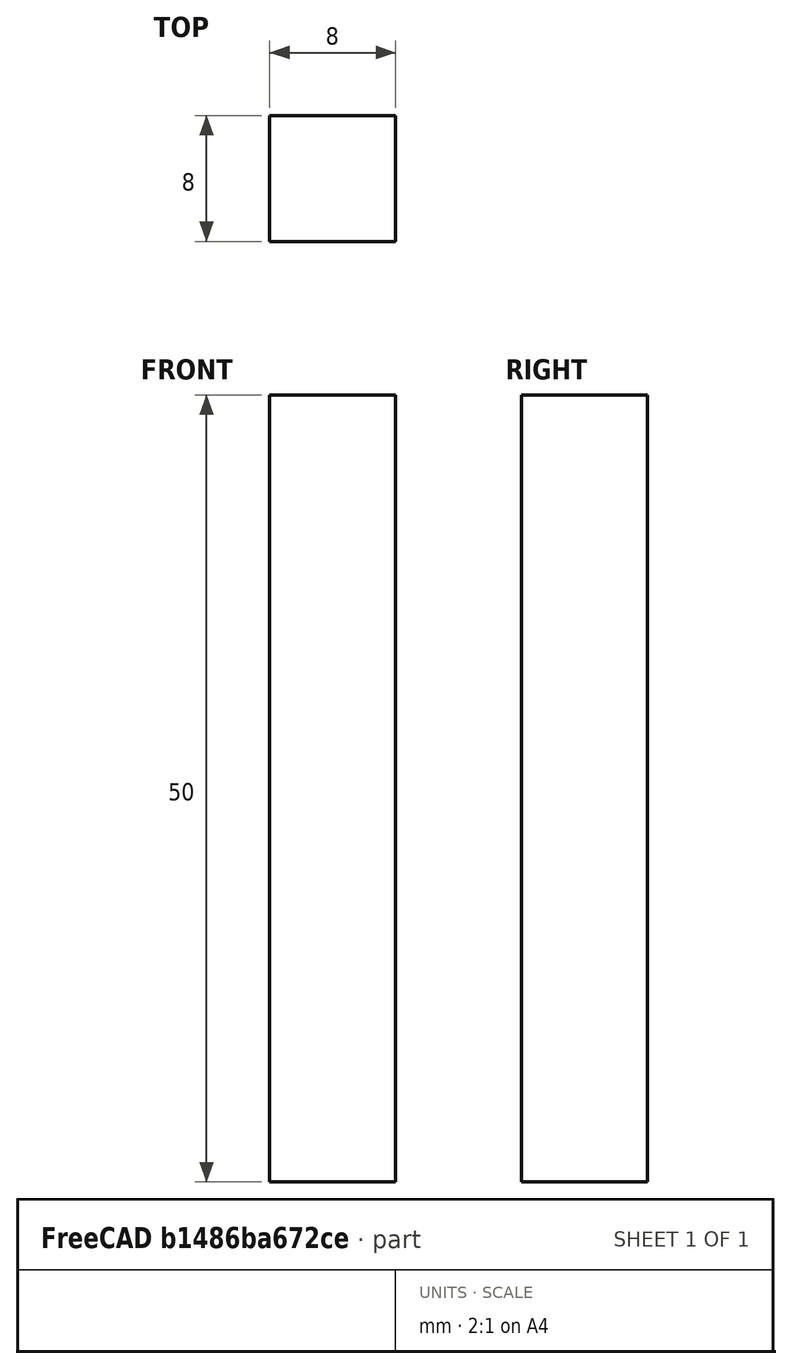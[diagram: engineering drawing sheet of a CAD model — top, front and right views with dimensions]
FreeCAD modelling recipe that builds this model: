
FCSTD DOCUMENT  (FreeCAD 0.15R4671 (Git))
Label: Square Bar 8 EN10059 S235JR
License: All rights reserved
LicenseURL: http://en.wikipedia.org/wiki/All_rights_reserved
objects: Sketcher::SketchObject×1, Part::Extrusion×1
note: 2 computed .brp shape members not serialized (recipe doc carries the construction recipe); baked Part::Feature solids carry a one-line shape summary decoded from their .brp

FEATURE [Sketcher::SketchObject] Sketch
  sketch-geometry (4):
    g0: LineSegment StartX=-4 StartY=-4 StartZ=0 EndX=4 EndY=-4 EndZ=0
    g1: LineSegment StartX=4 StartY=-4 StartZ=0 EndX=4 EndY=4 EndZ=0
    g2: LineSegment StartX=4 StartY=4 StartZ=0 EndX=-4 EndY=4 EndZ=0
    g3: LineSegment StartX=-4 StartY=4 StartZ=0 EndX=-4 EndY=-4 EndZ=0
  constraints (12):
    c: Coincident(g0,g1)
    c: Coincident(g1,g2)
    c: Coincident(g2,g3)
    c: Coincident(g3,g0)
    c: Horizontal(g0)
    c: Horizontal(g2)
    c: Vertical(g1)
    c: Vertical(g3)
    c: Symmetric(g1,g0,g-1)
    c: Symmetric(g2,g1,g-2)
    c: Equal(g1,g2)
    c: DistanceY(g1) = 8
FEATURE [Part::Extrusion] Extrude  label="Square Bar 8 EN10059 S235JR"
  Base = -> Sketch
  Dir = (0,0,50)
  Solid = true
